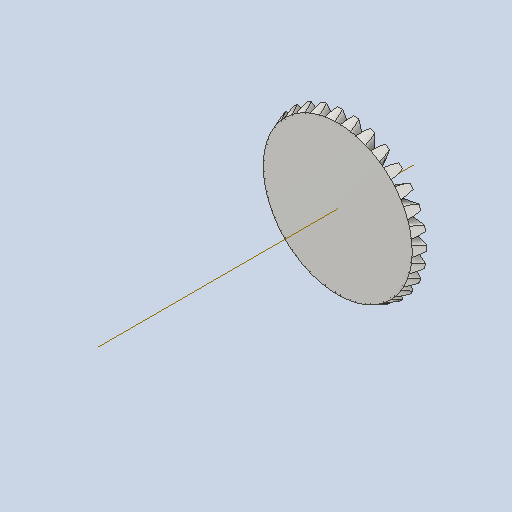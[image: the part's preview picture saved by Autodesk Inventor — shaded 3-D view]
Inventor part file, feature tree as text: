
AUTODESK INVENTOR PART (.ipt)
format: ipt  version: 2022 (Build 260153000, 153)  size: 614,912 bytes
history: native  units: in
note: dims shown in document units (in); Inventor stores cm internally (conversion verified against a paired STEP export)
features: other x30, sketch x1
ambient origin geometry x8: Origin, YZ Plane, XZ Plane, XY Plane, X Axis, Y Axis, Z Axis, Center Point
bodies: Solid1 (feature_tree)
feature tree (31):
  other  "Bevel Gear2"
  other  "Solid1::Bevel Gear2"
  other  "TaggingFeature1"
  other  "Teeth Body Sketch"
  other  "Start Sketch"
  other  "End Sketch"
  other  "End Sketch Right"
  other  "End Sketch Left"
  other  "Body Sketch"
  sketch  "Sketch6"  dims[d0=0.3937in d48=0.0in d49=0.0in d50=90.0deg d52=0.0in d53=0.0in d54=0.0in]
  other  "3D Sketch Right"
  other  "3D Sketch Left"
  other  "Mesh Plane"
  other  "Top Plane"
  other  "Mesh Plane2"
  other  "Tooth Plane"
  other  "End Plane"
  other  "End Plane Right"
  other  "End Plane Left"
  other  "Z Axis_1"
  other  "Top Point"
  other  "Start Point"
  other  "End Point"
  other  "Srf1"
  other  "Srf1::Derived"
  other  "Start plane iMate"
  other  "Mesh iMate2"
  other  "Axis Angle iMate"
  other  "Axis iMate"
  other  "Mesh iMate"
  other  "Intersection iMate"
